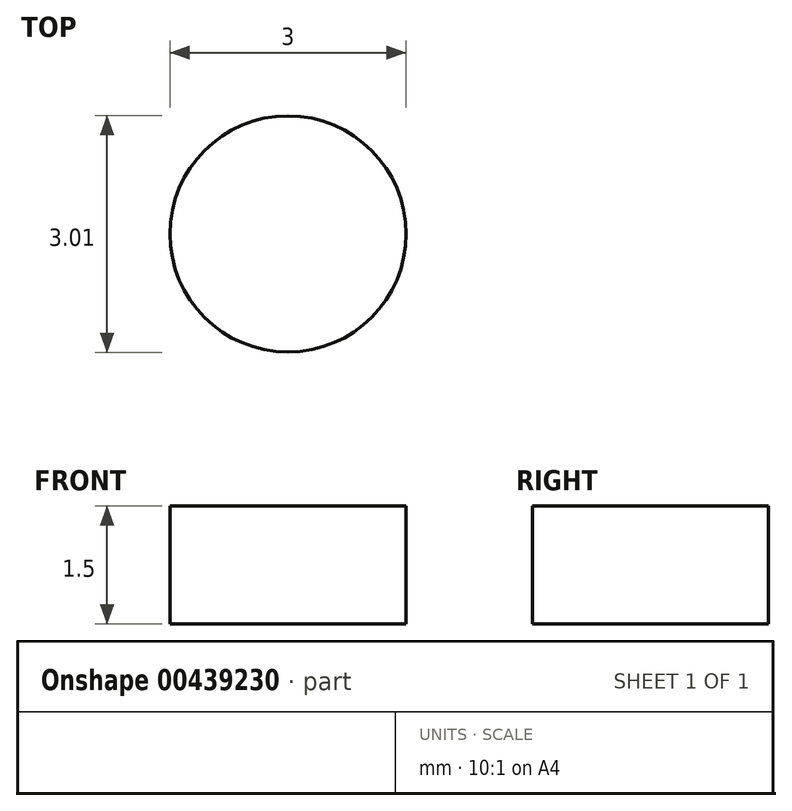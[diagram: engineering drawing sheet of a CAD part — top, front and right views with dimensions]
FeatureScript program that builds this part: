
annotation { "Feature Type Name" : "Feature", "Feature Type Description" : "" }
export const myFeature = defineFeature(function(context is Context, id is Id, definition is map)
    precondition{}
    {
        {
            var Q0;
            Q0=qCreatedBy(makeId("Top.planeOp"),FACE);
            var sketch = newSketch(context, id + "F0", { "sketchPlane" : qUnion([Q0])});
            skPoint(sketch, "E0.middle", {"position": v(0, 0) * mm});
            skCircle(sketch, "E1", {"center": v(-8.71, 7.17) * mm, "radius": 1.5 * mm});
            skCircle(sketch, "E2.MirrorC", {"center": v(8.71, 7.17) * mm, "radius": 1.5 * mm});
            skCircle(sketch, "E3.MirrorC", {"center": v(-8.71, -7.17) * mm, "radius": 1.5 * mm});
            skCircle(sketch, "E4.MirrorC", {"center": v(8.71, -7.17) * mm, "radius": 1.5 * mm});
            skArc(sketch, "E5.0", {"start": v(-5.56, 5.66) * mm, "mid": v(-11.16, 9.67) * mm, "end": v(-7.24, 4) * mm});
            skArc(sketch, "E6.MirrorC", {"start": v(5.56, 5.66) * mm, "mid": v(11.16, 9.67) * mm, "end": v(7.24, 4) * mm});
            skArc(sketch, "E7.MirrorC", {"start": v(-5.56, -5.66) * mm, "mid": v(-11.16, -9.67) * mm, "end": v(-7.24, -4) * mm});
            skArc(sketch, "E8.MirrorC", {"start": v(5.56, -5.66) * mm, "mid": v(11.16, -9.67) * mm, "end": v(7.24, -4) * mm});
            skPoint(sketch, "E9.orphan", {"position": v(8.7, 7.18) * mm});
            skPoint(sketch, "E10.orphan", {"position": v(8.71, -7.18) * mm});
            skPoint(sketch, "E11.trimOffspring.end.orphan", {"position": v(-8.71, -7.18) * mm});
            skFitSpline(sketch, "E12", {"points": [v(-5.56, 5.66) * mm, v(0, 3.17) * mm], "startDerivative": vector(4.38, -6.32) * mm, "endDerivative": vector(9.84, -0.42) * mm});
            skFitSpline(sketch, "E13.MirrorCS", {"points": [v(5.56, 5.66) * mm, v(0, 3.17) * mm], "startDerivative": vector(-4.38, -6.32) * mm, "endDerivative": vector(-9.84, -0.42) * mm});
            skFitSpline(sketch, "E14.MirrorCS", {"points": [v(-5.56, -5.66) * mm, v(0, -3.17) * mm], "startDerivative": vector(4.38, 6.32) * mm, "endDerivative": vector(9.84, 0.42) * mm});
            skFitSpline(sketch, "E15.MirrorCS", {"points": [v(5.56, -5.66) * mm, v(0, -3.17) * mm], "startDerivative": vector(-4.38, 6.32) * mm, "endDerivative": vector(-9.84, 0.42) * mm});
            skFitSpline(sketch, "E16", {"points": [v(-7.24, 4) * mm, v(-5.8, 0) * mm], "startDerivative": vector(3.12, -3.27) * mm, "endDerivative": vector(0.1, -8.92) * mm});
            skFitSpline(sketch, "E17.MirrorCS", {"points": [v(7.24, 4) * mm, v(5.8, 0) * mm], "startDerivative": vector(-3.12, -3.27) * mm, "endDerivative": vector(-0.1, -8.92) * mm});
            skFitSpline(sketch, "E18.MirrorCS", {"points": [v(7.24, -4) * mm, v(5.8, 0) * mm], "startDerivative": vector(-3.12, 3.27) * mm, "endDerivative": vector(-0.1, 8.92) * mm});
            skFitSpline(sketch, "E19.MirrorCS", {"points": [v(-7.24, -4) * mm, v(-5.8, 0) * mm], "startDerivative": vector(3.12, 3.27) * mm, "endDerivative": vector(0.1, 8.92) * mm});
            skSolve(sketch);
        }
        {
            var Q0;
            Q0=makeQuery(id+"F0.imprint","IMPRINT",FACE,{"disambiguationData":[TD([[makeQuery(id+"F0.imprint","IMPRINT",EDGE,{"derivedFrom":sQuery(id+"F0.wireOp",EDGE,"E2.MirrorC")}),1.0]])]});
            extrude(context, id + "F1", {"entities" : qUnion([Q0]), "depth" : 1.5 * mm, "offsetDistance" : 25 * mm});
        }
    });
